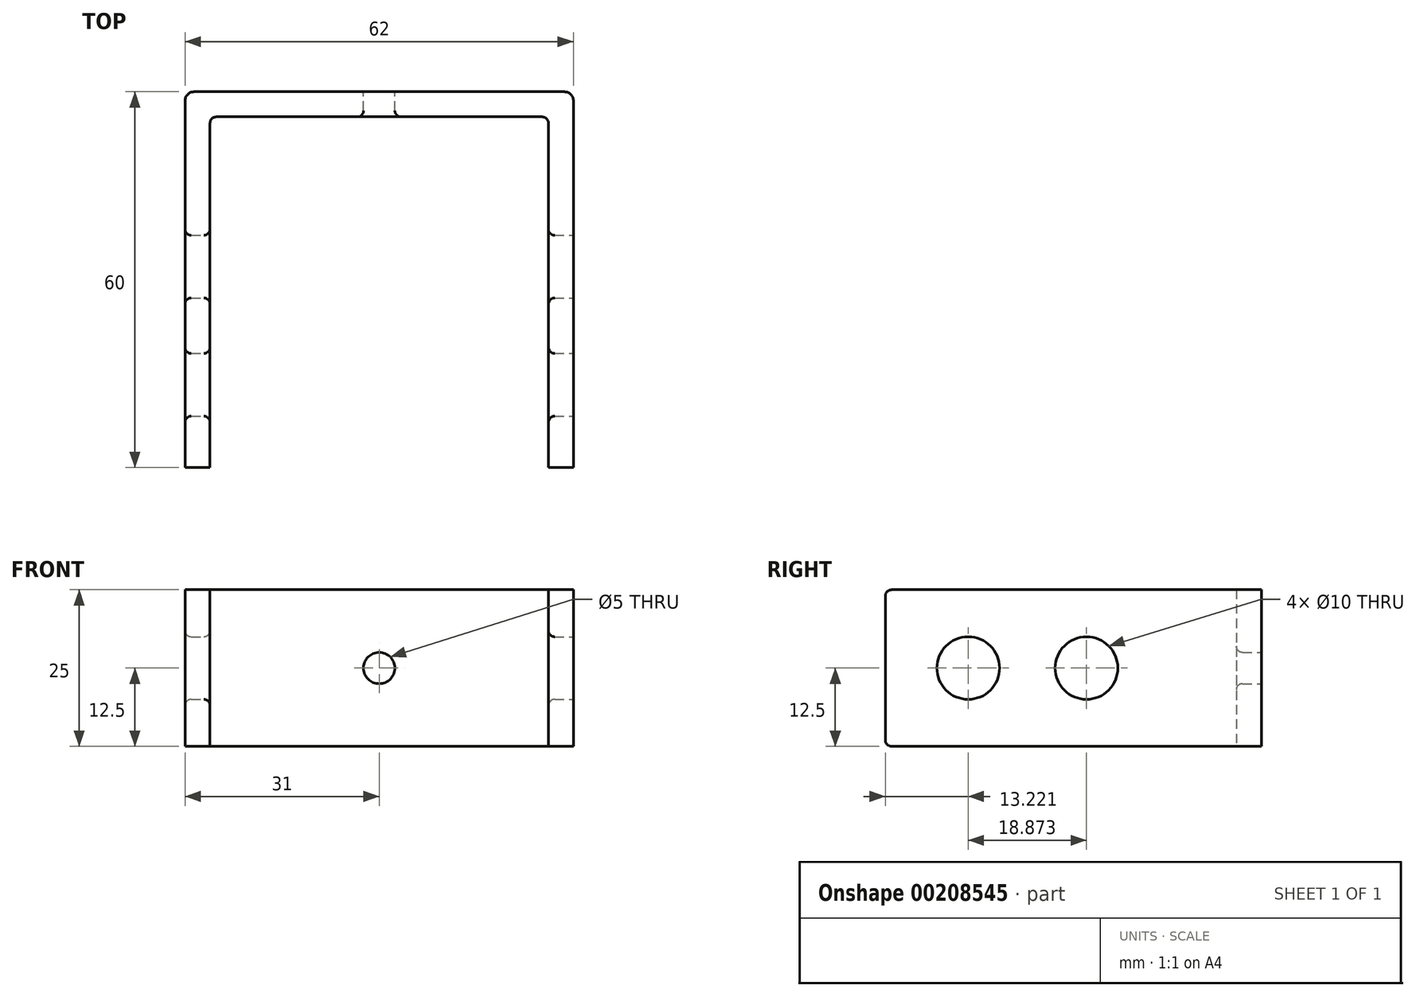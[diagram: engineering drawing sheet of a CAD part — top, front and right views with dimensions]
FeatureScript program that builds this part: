
annotation { "Feature Type Name" : "Feature", "Feature Type Description" : "" }
export const myFeature = defineFeature(function(context is Context, id is Id, definition is map)
    precondition{}
    {
        {
            var Q0;
            Q0=qCreatedBy(makeId("Top.planeOp"),FACE);
            var sketch = newSketch(context, id + "F0", { "sketchPlane" : qUnion([Q0])});
            skLineSegment(sketch, "E0", {"start": v(0, -60) * mm, "end": v(0, 0) * mm});
            skLineSegment(sketch, "E1", {"start": v(0, 0) * mm, "end": v(62, 0) * mm});
            skLineSegment(sketch, "E2", {"start": v(62, 0) * mm, "end": v(62, -60) * mm});
            skLineSegment(sketch, "E3", {"start": v(0, -60) * mm, "end": v(4, -60) * mm});
            skLineSegment(sketch, "E4", {"start": v(4, -60) * mm, "end": v(4, -4) * mm});
            skLineSegment(sketch, "E5", {"start": v(4, -4) * mm, "end": v(58, -4) * mm});
            skLineSegment(sketch, "E6", {"start": v(58, -4) * mm, "end": v(58, -60) * mm});
            skLineSegment(sketch, "E7", {"start": v(58, -60) * mm, "end": v(62, -60) * mm});
            skSolve(sketch);
        }
        {
            var Q0;
            Q0 = qSketchRegion(id + "F0", true);
            extrude(context, id + "F1", {"entities" : qUnion([Q0]), "depth" : 25 * mm});
        }
        {
            var Q0;
            Q0=makeQuery(id+"F1.opExtrude","SWEPT_FACE",FACE,{"disambiguationData":[OSD([sQuery(id+"F0.wireOp",EDGE,"E2")])]});
            var sketch = newSketch(context, id + "F2", { "sketchPlane" : qUnion([Q0])});
            skCircle(sketch, "E8", {"center": v(-46.78, 12.5) * mm, "radius": 5 * mm});
            skCircle(sketch, "E9", {"center": v(-27.9, 12.5) * mm, "radius": 5 * mm});
            skLineSegment(sketch, "E10", {"start": v(-69.3, 12.5) * mm, "end": v(10.36, 12.5) * mm, "construction": true});
            skSolve(sketch);
        }
        {
            var Q0;
            Q0 = qSketchRegion(id + "F2", true);
            extrude(context, id + "F3", {"entities" : qUnion([Q0]), "operationType" : NewBodyOperationType.REMOVE, "endBound" : BoundingType.THROUGH_ALL, "oppositeDirection" : true, "depth" : 25 * mm});
        }
        {
            var Q0;
            Q0=makeQuery(id+"F1.opExtrude","SWEPT_FACE",FACE,{"disambiguationData":[OSD([sQuery(id+"F0.wireOp",EDGE,"E1")])]});
            var sketch = newSketch(context, id + "F4", { "sketchPlane" : qUnion([Q0])});
            skCircle(sketch, "E11", {"center": v(-31, 12.5) * mm, "radius": 2.5 * mm});
            skLineSegment(sketch, "E12", {"start": v(-62, 0) * mm, "end": v(0, 25) * mm, "construction": true});
            skLineSegment(sketch, "E13", {"start": v(-62, 25) * mm, "end": v(0, 0) * mm, "construction": true});
            skSolve(sketch);
        }
        {
            var Q0;
            Q0 = qSketchRegion(id + "F4", true);
            extrude(context, id + "F5", {"entities" : qUnion([Q0]), "operationType" : NewBodyOperationType.REMOVE, "endBound" : BoundingType.THROUGH_ALL, "oppositeDirection" : true, "depth" : 25 * mm});
        }
        {
            var Q0;
            Q0=makeQuery(id+"F1.opExtrude","SWEPT_EDGE",EDGE,{"disambiguationData":[OSD([sQuery(id+"F0.wireOp",EDGE,"E1"),sQuery(id+"F0.wireOp",EDGE,"E2")])]});
            var Q1;
            Q1=makeQuery(id+"F1.opExtrude","SWEPT_EDGE",EDGE,{"disambiguationData":[OSD([sQuery(id+"F0.wireOp",EDGE,"E0"),sQuery(id+"F0.wireOp",EDGE,"E1")])]});
            fillet(context, id + "F6", {"entities" : qUnion([Q0, Q1]), "radius" : 1.45 * mm, "tangentPropagation" : true, "allowEdgeOverflow" : false});
        }
        {
            var Q0;
            Q0=makeQuery(id+"F1.opExtrude","SWEPT_EDGE",EDGE,{"disambiguationData":[OSD([sQuery(id+"F0.wireOp",EDGE,"E4"),sQuery(id+"F0.wireOp",EDGE,"E5")])]});
            var Q1;
            Q1=makeQuery(id+"F1.opExtrude","SWEPT_EDGE",EDGE,{"disambiguationData":[OSD([sQuery(id+"F0.wireOp",EDGE,"E5"),sQuery(id+"F0.wireOp",EDGE,"E6")])]});
            var Q2;
            Q2=makeQuery(id+"F3.boolean.opBoolean","COPY",EDGE,{"derivedFrom":makeQuery(id+"F3.opExtrude","CAP_EDGE",EDGE,{"disambiguationData":[OSD([sQuery(id+"F2.wireOp",EDGE,"E9")])],"isStart":true})});
            var Q3;
            Q3=makeQuery(id+"F3.boolean.opBoolean","COPY",EDGE,{"derivedFrom":makeQuery(id+"F3.opExtrude","CAP_EDGE",EDGE,{"disambiguationData":[OSD([sQuery(id+"F2.wireOp",EDGE,"E8")])],"isStart":true})});
            var Q4;
            Q4=makeQuery(id+"F3.boolean.opBoolean","INTERSECT",EDGE,{"derivedFrom":[makeQuery(id+"F1.opExtrude","SWEPT_FACE",FACE,{"disambiguationData":[OSD([sQuery(id+"F0.wireOp",EDGE,"E6")])]}),makeQuery(id+"F3.opExtrude","SWEPT_FACE",FACE,{"disambiguationData":[OSD([sQuery(id+"F2.wireOp",EDGE,"E8")])]})]});
            var Q5;
            Q5=makeQuery(id+"F3.boolean.opBoolean","INTERSECT",EDGE,{"derivedFrom":[makeQuery(id+"F1.opExtrude","SWEPT_FACE",FACE,{"disambiguationData":[OSD([sQuery(id+"F0.wireOp",EDGE,"E6")])]}),makeQuery(id+"F3.opExtrude","SWEPT_FACE",FACE,{"disambiguationData":[OSD([sQuery(id+"F2.wireOp",EDGE,"E9")])]})]});
            var Q6;
            Q6=makeQuery(id+"F3.boolean.opBoolean","INTERSECT",EDGE,{"derivedFrom":[makeQuery(id+"F1.opExtrude","SWEPT_FACE",FACE,{"disambiguationData":[OSD([sQuery(id+"F0.wireOp",EDGE,"E0")])]}),makeQuery(id+"F3.opExtrude","SWEPT_FACE",FACE,{"disambiguationData":[OSD([sQuery(id+"F2.wireOp",EDGE,"E9")])]})]});
            var Q7;
            Q7=makeQuery(id+"F3.boolean.opBoolean","INTERSECT",EDGE,{"derivedFrom":[makeQuery(id+"F1.opExtrude","SWEPT_FACE",FACE,{"disambiguationData":[OSD([sQuery(id+"F0.wireOp",EDGE,"E4")])]}),makeQuery(id+"F3.opExtrude","SWEPT_FACE",FACE,{"disambiguationData":[OSD([sQuery(id+"F2.wireOp",EDGE,"E9")])]})]});
            var Q8;
            Q8=makeQuery(id+"F3.boolean.opBoolean","INTERSECT",EDGE,{"derivedFrom":[makeQuery(id+"F1.opExtrude","SWEPT_FACE",FACE,{"disambiguationData":[OSD([sQuery(id+"F0.wireOp",EDGE,"E4")])]}),makeQuery(id+"F3.opExtrude","SWEPT_FACE",FACE,{"disambiguationData":[OSD([sQuery(id+"F2.wireOp",EDGE,"E8")])]})]});
            var Q9;
            Q9=makeQuery(id+"F3.boolean.opBoolean","INTERSECT",EDGE,{"derivedFrom":[makeQuery(id+"F1.opExtrude","SWEPT_FACE",FACE,{"disambiguationData":[OSD([sQuery(id+"F0.wireOp",EDGE,"E0")])]}),makeQuery(id+"F3.opExtrude","SWEPT_FACE",FACE,{"disambiguationData":[OSD([sQuery(id+"F2.wireOp",EDGE,"E8")])]})]});
            var Q10;
            Q10=makeQuery(id+"F5.boolean.opBoolean","COPY",EDGE,{"derivedFrom":makeQuery(id+"F5.opExtrude","CAP_EDGE",EDGE,{"disambiguationData":[OSD([sQuery(id+"F4.wireOp",EDGE,"E11")])],"isStart":true})});
            var Q11;
            Q11=makeQuery(id+"F5.boolean.opBoolean","INTERSECT",EDGE,{"derivedFrom":[makeQuery(id+"F1.opExtrude","SWEPT_FACE",FACE,{"disambiguationData":[OSD([sQuery(id+"F0.wireOp",EDGE,"E5")])]}),makeQuery(id+"F5.opExtrude","SWEPT_FACE",FACE,{"disambiguationData":[OSD([sQuery(id+"F4.wireOp",EDGE,"E11")])]})]});
            var Q12;
            Q12=makeQuery(id+"F1.opExtrude","CAP_EDGE",EDGE,{"disambiguationData":[OSD([sQuery(id+"F0.wireOp",EDGE,"E3")])],"isStart":false});
            var Q13;
            Q13=makeQuery(id+"F1.opExtrude","CAP_EDGE",EDGE,{"disambiguationData":[OSD([sQuery(id+"F0.wireOp",EDGE,"E7")])],"isStart":false});
            var Q14;
            Q14=makeQuery(id+"F1.opExtrude","CAP_EDGE",EDGE,{"disambiguationData":[OSD([sQuery(id+"F0.wireOp",EDGE,"E7")])],"isStart":true});
            var Q15;
            Q15=makeQuery(id+"F1.opExtrude","CAP_EDGE",EDGE,{"disambiguationData":[OSD([sQuery(id+"F0.wireOp",EDGE,"E3")])],"isStart":true});
            fillet(context, id + "F7", {"entities" : qUnion([Q0, Q1, Q2, Q3, Q4, Q5, Q6, Q7, Q8, Q9, Q10, Q11, Q12, Q13, Q14, Q15]), "radius" : 1 * mm, "tangentPropagation" : true, "allowEdgeOverflow" : false});
        }
    });
